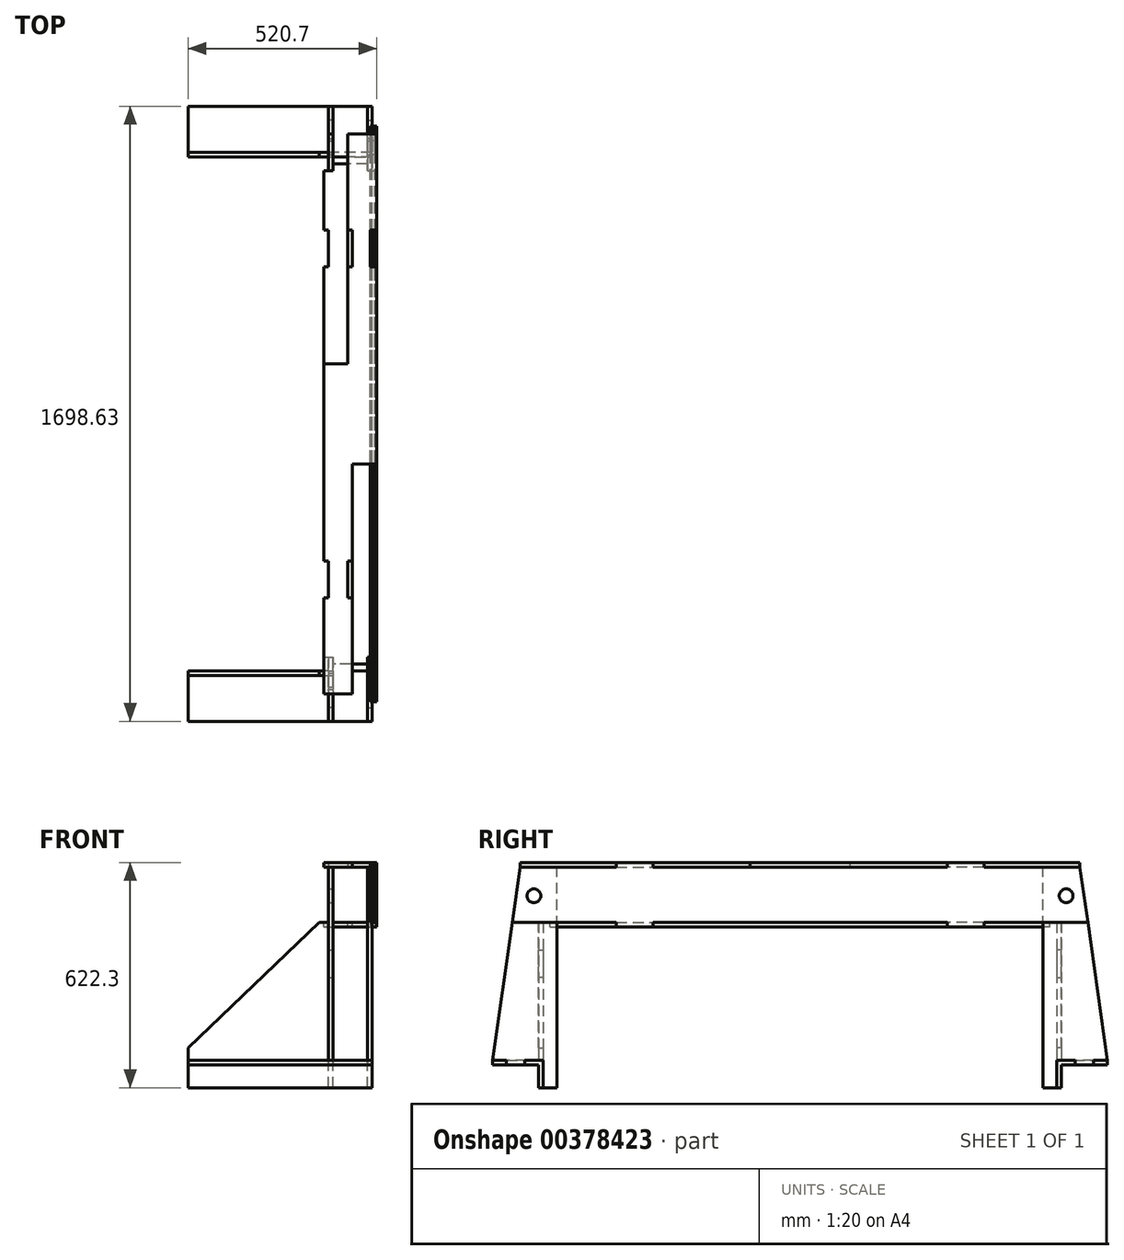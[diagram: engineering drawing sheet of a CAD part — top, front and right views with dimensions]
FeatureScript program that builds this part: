
annotation { "Feature Type Name" : "Feature", "Feature Type Description" : "" }
export const myFeature = defineFeature(function(context is Context, id is Id, definition is map)
    precondition{}
    {
        {
            var Q0;
            Q0=qCreatedBy(makeId("Top.planeOp"),FACE);
            var sketch = newSketch(context, id + "F0", { "sketchPlane" : qUnion([Q0])});
            skLineSegment(sketch, "E0", {"start": v(0, 0) * mm, "end": v(-508, 0) * mm});
            skLineSegment(sketch, "E1", {"start": v(-508, 0) * mm, "end": v(-508, 127) * mm});
            skLineSegment(sketch, "E2", {"start": v(-508, 127) * mm, "end": v(0, 127) * mm});
            skLineSegment(sketch, "E3", {"start": v(0, 127) * mm, "end": v(0, 0) * mm});
            skLineSegment(sketch, "E4.0", {"start": v(-12.7, 127) * mm, "end": v(-12.7, 0) * mm, "construction": true});
            skPoint(sketch, "E5", {"position": v(-12.7, 63.5) * mm});
            skPoint(sketch, "E6", {"position": v(-12.7, 38.1) * mm});
            skPoint(sketch, "E7", {"position": v(-12.7, 88.9) * mm});
            skLineSegment(sketch, "E8", {"start": v(-12.7, 88.9) * mm, "end": v(0, 88.9) * mm});
            skLineSegment(sketch, "E9", {"start": v(-12.7, 38.1) * mm, "end": v(0, 38.1) * mm});
            skLineSegment(sketch, "E10", {"start": v(-12.7, 88.9) * mm, "end": v(-12.7, 38.1) * mm});
            skLineSegment(sketch, "E11.0", {"start": v(-107.95, 127) * mm, "end": v(-107.95, 0) * mm, "construction": true});
            skLineSegment(sketch, "E12", {"start": v(-107.95, 88.9) * mm, "end": v(-107.95, 38.1) * mm, "construction": true});
            skLineSegment(sketch, "E13", {"start": v(-107.95, 88.9) * mm, "end": v(-120.65, 88.9) * mm});
            skLineSegment(sketch, "E14", {"start": v(-120.65, 88.9) * mm, "end": v(-120.65, 38.1) * mm});
            skLineSegment(sketch, "E15", {"start": v(-120.65, 38.1) * mm, "end": v(-107.95, 38.1) * mm});
            skLineSegment(sketch, "E16", {"start": v(-107.95, 88.9) * mm, "end": v(-107.95, 38.1) * mm});
            skSolve(sketch);
        }
        {
            var Q0;
            Q0=makeQuery(id+"F0.imprint","IMPRINT",FACE,{"disambiguationData":[TD([[makeQuery(id+"F0.imprint","IMPRINT",EDGE,{"derivedFrom":sQuery(id+"F0.wireOp",EDGE,"E0")}),-1.0]])]});
            extrude(context, id + "F1", {"entities" : qUnion([Q0]), "depth" : 12.7 * mm});
        }
        {
            var Q0;
            Q0=makeQuery(id+"F1.opExtrude","SWEPT_FACE",FACE,{"disambiguationData":[OSD([sQuery(id+"F0.wireOp",EDGE,"E0")])]});
            var sketch = newSketch(context, id + "F2", { "sketchPlane" : qUnion([Q0])});
            skLineSegment(sketch, "E17.0", {"start": v(0, 12.7) * mm, "end": v(-508, 12.7) * mm});
            skLineSegment(sketch, "E18", {"start": v(-508, 12.7) * mm, "end": v(-508, -63.5) * mm});
            skPoint(sketch, "E18.endSnap0", {"position": v(-508, 6.35) * mm});
            skLineSegment(sketch, "E19", {"start": v(-508, -63.5) * mm, "end": v(0, -63.5) * mm});
            skLineSegment(sketch, "E20", {"start": v(0, -63.5) * mm, "end": v(0, 12.7) * mm});
            skLineSegment(sketch, "E21.0", {"start": v(0, 0) * mm, "end": v(-508, 0) * mm, "construction": true});
            skPoint(sketch, "E22", {"position": v(-457.2, 0) * mm});
            skPoint(sketch, "E23", {"position": v(-381, 0) * mm});
            skPoint(sketch, "E24", {"position": v(-50.8, 0) * mm});
            skPoint(sketch, "E25", {"position": v(-127, 0) * mm});
            skLineSegment(sketch, "E26", {"start": v(-457.2, 0) * mm, "end": v(-381, 0) * mm});
            skLineSegment(sketch, "E27", {"start": v(-381, 0) * mm, "end": v(-381, 12.7) * mm});
            skLineSegment(sketch, "E28", {"start": v(-457.2, 0) * mm, "end": v(-457.2, 12.7) * mm});
            skLineSegment(sketch, "E29", {"start": v(-127, 0) * mm, "end": v(-50.8, 0) * mm});
            skLineSegment(sketch, "E30", {"start": v(-50.8, 0) * mm, "end": v(-50.8, 12.7) * mm});
            skLineSegment(sketch, "E31", {"start": v(-127, 0) * mm, "end": v(-127, 12.7) * mm});
            skSolve(sketch);
        }
        {
            var Q0;
            {var subQ3=sQuery(id+"F2.wireOp",EDGE,"E19");Q0=makeQuery(id+"F2.imprint","IMPRINT",FACE,{"disambiguationData":[TD([[makeQuery(id+"F2.imprint","IMPRINT",EDGE,{"derivedFrom":subQ3}),1.0]])]});}
            var Q1;
            {var subQ3=sQuery(id+"F2.wireOp",EDGE,"E28");Q1=makeQuery(id+"F2.imprint","IMPRINT",FACE,{"disambiguationData":[TD([[makeQuery(id+"F2.imprint","IMPRINT",EDGE,{"derivedFrom":subQ3}),1.0]])]});}
            var Q2;
            {var subQ3=sQuery(id+"F2.wireOp",EDGE,"E27");Q2=makeQuery(id+"F2.imprint","IMPRINT",FACE,{"disambiguationData":[TD([[makeQuery(id+"F2.imprint","IMPRINT",EDGE,{"derivedFrom":subQ3}),-1.0]])]});}
            var Q3;
            {var subQ3=sQuery(id+"F2.wireOp",EDGE,"E30");Q3=makeQuery(id+"F2.imprint","IMPRINT",FACE,{"disambiguationData":[TD([[makeQuery(id+"F2.imprint","IMPRINT",EDGE,{"derivedFrom":subQ3}),-1.0]])]});}
            extrude(context, id + "F3", {"entities" : qUnion([Q0, Q1, Q2, Q3]), "depth" : 12.7 * mm});
        }
        {
            var Q0;
            Q0=makeQuery(id+"F2.imprint","IMPRINT",FACE,{"disambiguationData":[TD([[makeQuery(id+"F2.imprint","IMPRINT",EDGE,{"derivedFrom":sQuery(id+"F2.wireOp",EDGE,"E26")}),-1.0]])]});
            var Q1;
            Q1=makeQuery(id+"F2.imprint","IMPRINT",FACE,{"disambiguationData":[TD([[makeQuery(id+"F2.imprint","IMPRINT",EDGE,{"derivedFrom":sQuery(id+"F2.wireOp",EDGE,"E29")}),-1.0]])]});
            var Q2;
            Q2=makeQuery(id+"F3.opExtrude","CAP_FACE",FACE,{"disambiguationData":[OSD([sQuery(id+"F2.wireOp",EDGE,"E17.0"),sQuery(id+"F2.wireOp",EDGE,"E18"),sQuery(id+"F2.wireOp",EDGE,"E19"),sQuery(id+"F2.wireOp",EDGE,"E20"),sQuery(id+"F2.wireOp",EDGE,"E26"),sQuery(id+"F2.wireOp",EDGE,"E27"),sQuery(id+"F2.wireOp",EDGE,"E28"),sQuery(id+"F2.wireOp",EDGE,"E29"),sQuery(id+"F2.wireOp",EDGE,"E30"),sQuery(id+"F2.wireOp",EDGE,"E31")])],"isStart":false});
            extrude(context, id + "F4", {"entities" : qUnion([Q0, Q1]), "operationType" : NewBodyOperationType.ADD, "endBound" : BoundingType.UP_TO_SURFACE, "endBoundEntityFace" : qUnion([Q2]), "depth" : 25.4 * mm});
        }
        {
            var Q0;
            Q0=makeQuery(id+"F1.opExtrude","SWEPT_FACE",FACE,{"disambiguationData":[OSD([sQuery(id+"F0.wireOp",EDGE,"E3")])]});
            var sketch = newSketch(context, id + "F5", { "sketchPlane" : qUnion([Q0])});
            skLineSegment(sketch, "E32.0", {"start": v(-12.7, -63.5) * mm, "end": v(-12.7, 12.7) * mm});
            skLineSegment(sketch, "E33.0", {"start": v(127, 12.7) * mm, "end": v(88.9, 12.7) * mm});
            skLineSegment(sketch, "E34", {"start": v(-12.7, 12.7) * mm, "end": v(38.1, 12.7) * mm});
            skLineSegment(sketch, "E35", {"start": v(-12.7, -63.5) * mm, "end": v(-50.8, -63.5) * mm});
            skLineSegment(sketch, "E36", {"start": v(-50.8, -63.5) * mm, "end": v(-50.8, 546.1) * mm});
            skLineSegment(sketch, "E37", {"start": v(-50.8, 546.1) * mm, "end": v(50.8, 546.1) * mm});
            skLineSegment(sketch, "E38", {"start": v(50.8, 546.1) * mm, "end": v(127, 12.7) * mm});
            skCircle(sketch, "E39", {"center": v(12.7, 466.73) * mm, "radius": 19.05 * mm});
            skLineSegment(sketch, "E40", {"start": v(12.7, 466.73) * mm, "end": v(-50.8, 466.73) * mm});
            skLineSegment(sketch, "E41", {"start": v(12.7, 466.73) * mm, "end": v(12.7, 546.1) * mm});
            skLineSegment(sketch, "E42.0", {"start": v(88.9, 0) * mm, "end": v(38.1, 0) * mm});
            skLineSegment(sketch, "E43", {"start": v(88.9, 0) * mm, "end": v(88.9, 12.7) * mm});
            skLineSegment(sketch, "E44", {"start": v(38.1, 0) * mm, "end": v(38.1, 12.7) * mm});
            skSolve(sketch);
        }
        {
            var Q0;
            Q0=makeQuery(id+"F5.imprint","IMPRINT",FACE,{"disambiguationData":[TD([[makeQuery(id+"F5.imprint","IMPRINT",EDGE,{"derivedFrom":sQuery(id+"F5.wireOp",EDGE,"E32.0")}),1.0]])]});
            var Q1;
            {var subQ1=sQuery(id+"F5.wireOp",EDGE,"E36");var subQ7=sQuery(id+"F5.wireOp",EDGE,"E37");var subQ8=makeQuery(id+"F5.imprint","INTERSECT",VERTEX,{"derivedFrom":[subQ1,subQ7]});Q1=makeQuery(id+"F5.imprint","IMPRINT",FACE,{"disambiguationData":[TD([[makeQuery(id+"F5.imprint","IMPRINT",EDGE,{"disambiguationData":[TD([[subQ8,1.0]])],"derivedFrom":subQ1}),-1.0]])]});}
            extrude(context, id + "F6", {"entities" : qUnion([Q0, Q1]), "oppositeDirection" : true, "depth" : 12.7 * mm});
        }
        {
            assignVariable(context, id + "F7", {"name" : "BW", "anyValue" : 4.25});
        }
        {
            var Q0;
            Q0=makeQuery(id+"F1.opExtrude","SWEPT_FACE",FACE,{"disambiguationData":[OSD([sQuery(id+"F0.wireOp",EDGE,"E16")])]});
            cPlane(context, id + "F8", {"entities" : qUnion([Q0]), "cplaneType" : CPlaneType.OFFSET, "offset" : 0 * mm, "oppositeDirection" : true, "width" : 152.4 * mm, "height" : 152.4 * mm});
        }
        {
            var Q0;
            Q0=qCreatedBy(id+"F8.planeOp",FACE);
            var sketch = newSketch(context, id + "F9", { "sketchPlane" : qUnion([Q0])});
            skLineSegment(sketch, "E45.0", {"start": v(50.8, 546.1) * mm, "end": v(-50.8, 546.1) * mm});
            skLineSegment(sketch, "E46.0", {"start": v(-50.8, 546.1) * mm, "end": v(-127, 12.7) * mm});
            skLineSegment(sketch, "E47.0", {"start": v(50.8, -63.5) * mm, "end": v(50.8, 546.1) * mm});
            skLineSegment(sketch, "E48.0", {"start": v(12.7, -63.5) * mm, "end": v(50.8, -63.5) * mm});
            skLineSegment(sketch, "E49.0", {"start": v(12.7, -63.5) * mm, "end": v(12.7, 12.7) * mm});
            skLineSegment(sketch, "E50.0", {"start": v(12.7, 12.7) * mm, "end": v(-38.1, 12.7) * mm});
            skPoint(sketch, "E51.0", {"position": v(-38.1, 6.35) * mm});
            skLineSegment(sketch, "E52.0", {"start": v(-88.9, 0) * mm, "end": v(-38.1, 0) * mm});
            skPoint(sketch, "E53.0", {"position": v(-88.9, 6.35) * mm});
            skLineSegment(sketch, "E54.0", {"start": v(-127, 12.7) * mm, "end": v(-88.9, 12.7) * mm});
            skLineSegment(sketch, "E55.0", {"start": v(-88.9, 0) * mm, "end": v(-88.9, 12.7) * mm});
            skLineSegment(sketch, "E56.0", {"start": v(-38.1, 0) * mm, "end": v(-38.1, 12.7) * mm});
            skLineSegment(sketch, "E57", {"start": v(12.7, 12.7) * mm, "end": v(12.7, 546.1) * mm, "construction": true});
            skLineSegment(sketch, "E58.0", {"start": v(0, 12.7) * mm, "end": v(0, 546.1) * mm, "construction": true});
            skPoint(sketch, "E59", {"position": v(12.7, 241.3) * mm});
            skLineSegment(sketch, "E60", {"start": v(12.7, 241.3) * mm, "end": v(0, 241.3) * mm});
            skPoint(sketch, "E60.endSnap0", {"position": v(0, 279.4) * mm});
            skLineSegment(sketch, "E61", {"start": v(0, 241.3) * mm, "end": v(0, 317.5) * mm});
            skLineSegment(sketch, "E62", {"start": v(0, 317.5) * mm, "end": v(12.7, 317.5) * mm});
            skLineSegment(sketch, "E63", {"start": v(12.7, 317.5) * mm, "end": v(12.7, 241.3) * mm});
            skCircle(sketch, "E64.0", {"center": v(-12.7, 466.73) * mm, "radius": 19.05 * mm});
            skSolve(sketch);
        }
        {
            var Q0;
            Q0=makeQuery(id+"F9.imprint","IMPRINT",FACE,{"disambiguationData":[TD([[makeQuery(id+"F9.imprint","IMPRINT",EDGE,{"derivedFrom":sQuery(id+"F9.wireOp",EDGE,"E45.0")}),1.0]])]});
            extrude(context, id + "F10", {"entities" : qUnion([Q0]), "depth" : 12.7 * mm});
        }
        {
            var Q0;
            {var subQ0=sQuery(id+"F2.wireOp",EDGE,"E17.0");Q0=makeQuery(id+"F3.opExtrude","SWEPT_FACE",FACE,{"disambiguationData":[OSD([subQ0]),TDD([makeQuery(id+"F2.imprint","IMPRINT",EDGE,{"disambiguationData":[TD([[makeQuery(id+"F2.imprint","INTERSECT",VERTEX,{"derivedFrom":[subQ0,sQuery(id+"F2.wireOp",EDGE,"E27")]}),1.0]])],"derivedFrom":subQ0})])]});}
            var sketch = newSketch(context, id + "F11", { "sketchPlane" : qUnion([Q0])});
            skLineSegment(sketch, "E65.0", {"start": v(-120.65, -12.7) * mm, "end": v(-120.65, 38.1) * mm});
            skLineSegment(sketch, "E66.0", {"start": v(-508, -12.7) * mm, "end": v(-508, 0) * mm});
            skLineSegment(sketch, "E67", {"start": v(-508, -12.7) * mm, "end": v(-120.65, -12.7) * mm});
            skLineSegment(sketch, "E68", {"start": v(-508, 0) * mm, "end": v(-120.65, 0) * mm});
            skSolve(sketch);
        }
        {
            var Q0;
            Q0=makeQuery(id+"F11.imprint","IMPRINT",FACE,{"disambiguationData":[TD([[makeQuery(id+"F11.imprint","IMPRINT",EDGE,{"derivedFrom":sQuery(id+"F11.wireOp",EDGE,"c8208c28-5663-4249-825d-4aff4fe314d8.0")}),1.0]])]});
            var Q1;
            {var subQ1=sQuery(id+"F2.wireOp",EDGE,"E17.0");var subQ2=makeQuery(id+"F3.opExtrude","SWEPT_EDGE",EDGE,{"disambiguationData":[OSD([subQ1,sQuery(id+"F2.wireOp",EDGE,"E27")])]});Q1=makeQuery(id+"F11.imprint","IMPRINT",FACE,{"disambiguationData":[TD([[makeQuery(id+"F11.imprint","IMPRINT",EDGE,{"derivedFrom":subQ2}),-1.0]])]});}
            var Q2;
            {var subQ0=sQuery(id+"F11.wireOp",EDGE,"E66.0");Q2=makeQuery(id+"F11.imprint","IMPRINT",FACE,{"disambiguationData":[TD([[makeQuery(id+"F11.imprint","IMPRINT",EDGE,{"derivedFrom":subQ0}),-1.0]])]});}
            var Q3;
            {var subQ5=makeQuery(id+"F3.opExtrude","SWEPT_EDGE",EDGE,{"disambiguationData":[OSD([sQuery(id+"F2.wireOp",EDGE,"E17.0"),sQuery(id+"F2.wireOp",EDGE,"E31")])]});Q3=makeQuery(id+"F11.imprint","IMPRINT",FACE,{"disambiguationData":[TD([[makeQuery(id+"F11.imprint","IMPRINT",EDGE,{"derivedFrom":subQ5}),-1.0]])]});}
            extrude(context, id + "F12", {"entities" : qUnion([Q0, Q1, Q2, Q3]), "depth" : 381 * mm});
        }
        {
            var Q0;
            Q0=makeQuery(id+"F12.opExtrude","SWEPT_FACE",FACE,{"disambiguationData":[OSD([sQuery(id+"F11.wireOp",EDGE,"E67")])]});
            var sketch = newSketch(context, id + "F13", { "sketchPlane" : qUnion([Q0])});
            skLineSegment(sketch, "E69.0", {"start": v(-508, 12.7) * mm, "end": v(-120.65, 12.7) * mm});
            skLineSegment(sketch, "E70", {"start": v(-508, 12.7) * mm, "end": v(-508, 46.36) * mm});
            skLineSegment(sketch, "E71", {"start": v(-120.65, 393.7) * mm, "end": v(-146.05, 393.7) * mm});
            skLineSegment(sketch, "E72", {"start": v(-146.05, 393.7) * mm, "end": v(-508, 46.36) * mm});
            skSolve(sketch);
        }
        {
            var Q0;
            Q0=makeQuery(id+"F9.imprint","IMPRINT",FACE,{"disambiguationData":[TD([[makeQuery(id+"F9.imprint","IMPRINT",EDGE,{"derivedFrom":sQuery(id+"F9.wireOp",EDGE,"E60")}),-1.0]])]});
            extrude(context, id + "F14", {"entities" : qUnion([Q0]), "endBound" : BoundingType.UP_TO_NEXT, "depth" : 25.4 * mm});
        }
        {
            var Q0;
            {var subQ0=sQuery(id+"F13.wireOp",EDGE,"E72");Q0=makeQuery(id+"F13.imprint","IMPRINT",FACE,{"disambiguationData":[TD([[makeQuery(id+"F13.imprint","IMPRINT",EDGE,{"derivedFrom":subQ0}),-1.0]])]});}
            extrude(context, id + "F15", {"entities" : qUnion([Q0]), "operationType" : NewBodyOperationType.REMOVE, "oppositeDirection" : true, "depth" : 25.4 * mm});
        }
        {
            var Q0;
            Q0=makeQuery(id+"F5.imprint","IMPRINT",FACE,{"disambiguationData":[TD([[makeQuery(id+"F5.imprint","IMPRINT",EDGE,{"derivedFrom":sQuery(id+"F5.wireOp",EDGE,"E39")}),1.0]])]});
            extrude(context, id + "F16", {"entities" : qUnion([Q0]), "oppositeDirection" : true, "depth" : (getVariable(context, 'BW') + 1) * mm});
        }
        {
            var Q0;
            Q0=qCreatedBy(makeId("Front.planeOp"),FACE);
            cPlane(context, id + "F17", {"entities" : qUnion([Q0]), "cplaneType" : CPlaneType.OFFSET, "offset" : 722.3 * mm, "width" : 152.4 * mm, "height" : 152.4 * mm});
        }
        {
            var Q0;
            Q0=makeQuery(id+"F1.opExtrude","SWEPT_BODY",BODY,{"disambiguationData":[OSD([sQuery(id+"F0.wireOp",EDGE,"E0"),sQuery(id+"F0.wireOp",EDGE,"E1"),sQuery(id+"F0.wireOp",EDGE,"E2"),sQuery(id+"F0.wireOp",EDGE,"E3"),sQuery(id+"F0.wireOp",EDGE,"E8"),sQuery(id+"F0.wireOp",EDGE,"E9"),sQuery(id+"F0.wireOp",EDGE,"E10"),sQuery(id+"F0.wireOp",EDGE,"E13"),sQuery(id+"F0.wireOp",EDGE,"E14"),sQuery(id+"F0.wireOp",EDGE,"E15"),sQuery(id+"F0.wireOp",EDGE,"E16")])]});
            var Q1;
            Q1=makeQuery(id+"F16.opExtrude","SWEPT_BODY",BODY,{"disambiguationData":[OSD([sQuery(id+"F5.wireOp",EDGE,"E39")])]});
            var Q2;
            Q2=makeQuery(id+"F10.opExtrude","SWEPT_BODY",BODY,{"disambiguationData":[OSD([sQuery(id+"F9.wireOp",EDGE,"E45.0"),sQuery(id+"F9.wireOp",EDGE,"E46.0"),sQuery(id+"F9.wireOp",EDGE,"E47.0"),sQuery(id+"F9.wireOp",EDGE,"E48.0"),sQuery(id+"F9.wireOp",EDGE,"E49.0"),sQuery(id+"F9.wireOp",EDGE,"E50.0"),sQuery(id+"F9.wireOp",EDGE,"E52.0"),sQuery(id+"F9.wireOp",EDGE,"E54.0"),sQuery(id+"F9.wireOp",EDGE,"E55.0"),sQuery(id+"F9.wireOp",EDGE,"E56.0")])]});
            var Q3;
            Q3=makeQuery(id+"F12.opExtrude","SWEPT_BODY",BODY,{"disambiguationData":[OSD([sQuery(id+"F11.wireOp",EDGE,"E65.0"),sQuery(id+"F11.wireOp",EDGE,"E66.0"),sQuery(id+"F11.wireOp",EDGE,"E67"),sQuery(id+"F11.wireOp",EDGE,"E68")])]});
            var Q4;
            Q4=makeQuery(id+"F6.opExtrude","SWEPT_BODY",BODY,{"disambiguationData":[OSD([sQuery(id+"F5.wireOp",EDGE,"E32.0"),sQuery(id+"F5.wireOp",EDGE,"E33.0"),sQuery(id+"F5.wireOp",EDGE,"E34"),sQuery(id+"F5.wireOp",EDGE,"E35"),sQuery(id+"F5.wireOp",EDGE,"E36"),sQuery(id+"F5.wireOp",EDGE,"E37"),sQuery(id+"F5.wireOp",EDGE,"E38"),sQuery(id+"F5.wireOp",EDGE,"E39"),sQuery(id+"F5.wireOp",EDGE,"E42.0"),sQuery(id+"F5.wireOp",EDGE,"E43"),sQuery(id+"F5.wireOp",EDGE,"E44")])]});
            var Q5;
            Q5=makeQuery(id+"F3.opExtrude","SWEPT_BODY",BODY,{"disambiguationData":[OSD([sQuery(id+"F2.wireOp",EDGE,"E17.0"),sQuery(id+"F2.wireOp",EDGE,"E18"),sQuery(id+"F2.wireOp",EDGE,"E19"),sQuery(id+"F2.wireOp",EDGE,"E20"),sQuery(id+"F2.wireOp",EDGE,"E26"),sQuery(id+"F2.wireOp",EDGE,"E27"),sQuery(id+"F2.wireOp",EDGE,"E28"),sQuery(id+"F2.wireOp",EDGE,"E29"),sQuery(id+"F2.wireOp",EDGE,"E30"),sQuery(id+"F2.wireOp",EDGE,"E31")])]});
            var Q6;
            Q6=qCreatedBy(id+"F17.planeOp",FACE);
            mirror(context, id + "F18", {"entities" : qUnion([Q0, Q1, Q2, Q3, Q4, Q5]), "mirrorPlane" : qUnion([Q6])});
        }
        {
            var Q0;
            Q0=makeQuery(id+"F18.opPattern","COPY",FACE,{"derivedFrom":makeQuery(id+"F6.opExtrude","CAP_FACE",FACE,{"disambiguationData":[OSD([sQuery(id+"F5.wireOp",EDGE,"E32.0"),sQuery(id+"F5.wireOp",EDGE,"E33.0"),sQuery(id+"F5.wireOp",EDGE,"E34"),sQuery(id+"F5.wireOp",EDGE,"E35"),sQuery(id+"F5.wireOp",EDGE,"E36"),sQuery(id+"F5.wireOp",EDGE,"E37"),sQuery(id+"F5.wireOp",EDGE,"E38"),sQuery(id+"F5.wireOp",EDGE,"E39")])],"isStart":true}),"instanceName":"1"});
            var sketch = newSketch(context, id + "F19", { "sketchPlane" : qUnion([Q0])});
            skLineSegment(sketch, "E73.0", {"start": v(-1495.42, 546.1) * mm, "end": v(-1517.2, 393.7) * mm});
            skLineSegment(sketch, "E74.0", {"start": v(50.8, 546.1) * mm, "end": v(72.57, 393.7) * mm});
            skCircle(sketch, "E75.0", {"center": v(12.7, 466.73) * mm, "radius": 19.05 * mm});
            skCircle(sketch, "E76.0", {"center": v(-1457.33, 466.73) * mm, "radius": 19.05 * mm});
            skLineSegment(sketch, "E77", {"start": v(-1495.42, 546.1) * mm, "end": v(50.8, 546.1) * mm});
            skLineSegment(sketch, "E78.0", {"start": v(-1517.2, 393.7) * mm, "end": v(72.57, 393.7) * mm});
            skPoint(sketch, "E79.orphan", {"position": v(-1571.62, 12.7) * mm});
            skPoint(sketch, "E80.orphan", {"position": v(127, 12.7) * mm});
            skLineSegment(sketch, "E81.0", {"start": v(-1230.31, 558.8) * mm, "end": v(-1128.71, 558.8) * mm});
            skLineSegment(sketch, "E82.0", {"start": v(-1230.31, 381) * mm, "end": v(-1128.71, 381) * mm});
            skLineSegment(sketch, "E83", {"start": v(-722.31, 546.1) * mm, "end": v(-722.31, 393.7) * mm, "construction": true});
            skLineSegment(sketch, "E84", {"start": v(-722.31, 469.9) * mm, "end": v(-315.91, 469.9) * mm, "construction": true});
            skLineSegment(sketch, "E85", {"start": v(-315.91, 469.9) * mm, "end": v(-722.31, 469.9) * mm, "construction": true});
            skLineSegment(sketch, "E86", {"start": v(-722.31, 469.9) * mm, "end": v(-1128.71, 469.9) * mm, "construction": true});
            skLineSegment(sketch, "E87", {"start": v(-315.91, 469.9) * mm, "end": v(-265.11, 469.9) * mm, "construction": true});
            skLineSegment(sketch, "E88", {"start": v(-265.11, 469.9) * mm, "end": v(-214.31, 469.9) * mm, "construction": true});
            skLineSegment(sketch, "E89", {"start": v(-1128.71, 469.9) * mm, "end": v(-1179.51, 469.9) * mm, "construction": true});
            skLineSegment(sketch, "E90", {"start": v(-1179.51, 469.9) * mm, "end": v(-1230.31, 469.9) * mm, "construction": true});
            skLineSegment(sketch, "E91", {"start": v(-214.31, 469.9) * mm, "end": v(-214.31, 558.8) * mm});
            skLineSegment(sketch, "E92", {"start": v(-315.91, 469.9) * mm, "end": v(-315.91, 558.8) * mm});
            skLineSegment(sketch, "E93", {"start": v(-315.91, 469.9) * mm, "end": v(-315.91, 381) * mm});
            skLineSegment(sketch, "E94", {"start": v(-214.31, 469.9) * mm, "end": v(-214.31, 381) * mm});
            skLineSegment(sketch, "E95", {"start": v(-1230.31, 469.9) * mm, "end": v(-1230.31, 558.8) * mm});
            skLineSegment(sketch, "E96", {"start": v(-1128.71, 469.9) * mm, "end": v(-1128.71, 558.8) * mm});
            skLineSegment(sketch, "E97", {"start": v(-1128.71, 469.9) * mm, "end": v(-1128.71, 381) * mm});
            skLineSegment(sketch, "E98", {"start": v(-1230.31, 469.9) * mm, "end": v(-1230.31, 381) * mm});
            skLineSegment(sketch, "E99.trimOffspring", {"start": v(-315.91, 558.8) * mm, "end": v(-214.31, 558.8) * mm});
            skLineSegment(sketch, "E100.trimOffspring", {"start": v(-315.91, 381) * mm, "end": v(-214.31, 381) * mm});
            skSolve(sketch);
        }
        {
            var Q0;
            {var subQ1=sQuery(id+"F19.wireOp",EDGE,"E74.0");Q0=makeQuery(id+"F19.imprint","IMPRINT",FACE,{"disambiguationData":[TD([[makeQuery(id+"F19.imprint","IMPRINT",EDGE,{"derivedFrom":subQ1}),-1.0]])]});}
            var Q1;
            {var subQ1=sQuery(id+"F19.wireOp",EDGE,"E73.0");Q1=makeQuery(id+"F19.imprint","IMPRINT",FACE,{"disambiguationData":[TD([[makeQuery(id+"F19.imprint","IMPRINT",EDGE,{"derivedFrom":subQ1}),1.0]])]});}
            var Q2;
            {var subQ1=sQuery(id+"F19.wireOp",EDGE,"E92");var subQ3=sQuery(id+"F19.wireOp",EDGE,"E77");var subQ4=makeQuery(id+"F19.imprint","INTERSECT",VERTEX,{"derivedFrom":[subQ3,subQ1]});Q2=makeQuery(id+"F19.imprint","IMPRINT",FACE,{"disambiguationData":[TD([[makeQuery(id+"F19.imprint","IMPRINT",EDGE,{"disambiguationData":[TD([[subQ4,-1.0]])],"derivedFrom":subQ3}),-1.0]])]});}
            var Q3;
            {var subQ5=sQuery(id+"F19.wireOp",EDGE,"E99.trimOffspring");Q3=makeQuery(id+"F19.imprint","IMPRINT",FACE,{"disambiguationData":[TD([[makeQuery(id+"F19.imprint","IMPRINT",EDGE,{"derivedFrom":subQ5}),-1.0]])]});}
            var Q4;
            {var subQ5=sQuery(id+"F19.wireOp",EDGE,"E100.trimOffspring");Q4=makeQuery(id+"F19.imprint","IMPRINT",FACE,{"disambiguationData":[TD([[makeQuery(id+"F19.imprint","IMPRINT",EDGE,{"derivedFrom":subQ5}),1.0]])]});}
            var Q5;
            {var subQ7=sQuery(id+"F19.wireOp",EDGE,"E77");var subQ9=sQuery(id+"F19.wireOp",EDGE,"E96");var subQ10=makeQuery(id+"F19.imprint","INTERSECT",VERTEX,{"derivedFrom":[subQ7,subQ9]});Q5=makeQuery(id+"F19.imprint","IMPRINT",FACE,{"disambiguationData":[TD([[makeQuery(id+"F19.imprint","IMPRINT",EDGE,{"disambiguationData":[TD([[subQ10,-1.0]])],"derivedFrom":subQ7}),-1.0]])]});}
            var Q6;
            {var subQ1=sQuery(id+"F19.wireOp",EDGE,"E95");var subQ3=sQuery(id+"F19.wireOp",EDGE,"E77");var subQ4=makeQuery(id+"F19.imprint","INTERSECT",VERTEX,{"derivedFrom":[subQ3,subQ1]});Q6=makeQuery(id+"F19.imprint","IMPRINT",FACE,{"disambiguationData":[TD([[makeQuery(id+"F19.imprint","IMPRINT",EDGE,{"disambiguationData":[TD([[subQ4,-1.0]])],"derivedFrom":subQ3}),-1.0]])]});}
            var Q7;
            {var subQ5=sQuery(id+"F19.wireOp",EDGE,"E81.0");Q7=makeQuery(id+"F19.imprint","IMPRINT",FACE,{"disambiguationData":[TD([[makeQuery(id+"F19.imprint","IMPRINT",EDGE,{"derivedFrom":subQ5}),-1.0]])]});}
            var Q8;
            {var subQ5=sQuery(id+"F19.wireOp",EDGE,"E82.0");Q8=makeQuery(id+"F19.imprint","IMPRINT",FACE,{"disambiguationData":[TD([[makeQuery(id+"F19.imprint","IMPRINT",EDGE,{"derivedFrom":subQ5}),1.0]])]});}
            var Q9;
            {var subQ1=sQuery(id+"F19.wireOp",EDGE,"E95");var subQ5=sQuery(id+"F19.wireOp",EDGE,"E77");var subQ9=makeQuery(id+"F19.imprint","INTERSECT",VERTEX,{"derivedFrom":[subQ5,subQ1]});Q9=makeQuery(id+"F19.imprint","IMPRINT",FACE,{"disambiguationData":[TD([[makeQuery(id+"F19.imprint","IMPRINT",EDGE,{"disambiguationData":[TD([[subQ9,1.0]])],"derivedFrom":subQ5}),-1.0]])]});}
            extrude(context, id + "F20", {"entities" : qUnion([Q0, Q1, Q2, Q3, Q4, Q5, Q6, Q7, Q8, Q9]), "depth" : 12.7 * mm});
        }
        {
            var Q0;
            Q0=makeQuery(id+"F20.opExtrude","SWEPT_BODY",BODY,{"disambiguationData":[OSD([sQuery(id+"F19.wireOp",EDGE,"E73.0"),sQuery(id+"F19.wireOp",EDGE,"E74.0"),sQuery(id+"F19.wireOp",EDGE,"E75.0"),sQuery(id+"F19.wireOp",EDGE,"E76.0"),sQuery(id+"F19.wireOp",EDGE,"E77"),sQuery(id+"F19.wireOp",EDGE,"E78.0")])]});
            transform(context, id + "F21", {"entities" : qUnion([Q0]), "transformType" : TransformType.TRANSLATION_3D, "dx" : (-getVariable(context, 'BW') - 1) * mm, "dy" : 0 * mm, "dz" : 0 * mm, "makeCopy" : true});
        }
        {
            var Q0;
            Q0=makeQuery(id+"F20.opExtrude","SWEPT_FACE",FACE,{"disambiguationData":[OSD([sQuery(id+"F19.wireOp",EDGE,"E77")])]});
            var sketch = newSketch(context, id + "F22", { "sketchPlane" : qUnion([Q0])});
            skLineSegment(sketch, "E101.0", {"start": v(-133.35, -1230.31) * mm, "end": v(-133.35, -1495.42) * mm});
            skLineSegment(sketch, "E102.0", {"start": v(12.7, -214.31) * mm, "end": v(12.7, 50.8) * mm});
            skLineSegment(sketch, "E103", {"start": v(-133.35, -1495.42) * mm, "end": v(-53.97, -1495.42) * mm});
            skLineSegment(sketch, "E104", {"start": v(12.7, 50.8) * mm, "end": v(-66.68, 50.8) * mm});
            skLineSegment(sketch, "E105", {"start": v(-53.97, -1495.42) * mm, "end": v(-53.98, -860.42) * mm});
            skLineSegment(sketch, "E106", {"start": v(-66.68, 50.8) * mm, "end": v(-66.67, -584.2) * mm});
            skLineSegment(sketch, "E107", {"start": v(-66.67, -584.2) * mm, "end": v(-133.35, -584.2) * mm});
            skLineSegment(sketch, "E108", {"start": v(-53.98, -860.42) * mm, "end": v(12.7, -860.42) * mm});
            skLineSegment(sketch, "E109", {"start": v(12.7, -860.42) * mm, "end": v(12.7, -315.91) * mm});
            skLineSegment(sketch, "E110", {"start": v(-133.35, -1128.71) * mm, "end": v(-133.35, -584.2) * mm});
            skLineSegment(sketch, "E111.0.1", {"start": v(-133.35, -1230.31) * mm, "end": v(-120.65, -1230.31) * mm});
            skLineSegment(sketch, "E111.0.2", {"start": v(-120.65, -1230.31) * mm, "end": v(-120.65, -1128.71) * mm});
            skLineSegment(sketch, "E111.0.3", {"start": v(-120.65, -1128.71) * mm, "end": v(-133.35, -1128.71) * mm});
            skLineSegment(sketch, "E112.0.0", {"start": v(0, -214.31) * mm, "end": v(0, -315.91) * mm});
            skLineSegment(sketch, "E112.0.1", {"start": v(0, -315.91) * mm, "end": v(12.7, -315.91) * mm});
            skLineSegment(sketch, "E112.0.3", {"start": v(12.7, -214.31) * mm, "end": v(0, -214.31) * mm});
            skLineSegment(sketch, "E113.0", {"start": v(-66.68, -1230.31) * mm, "end": v(-66.68, -1128.71) * mm});
            skLineSegment(sketch, "E114.0", {"start": v(-53.97, -214.31) * mm, "end": v(-53.97, -315.91) * mm});
            skLineSegment(sketch, "E115", {"start": v(-66.68, -1128.71) * mm, "end": v(-53.98, -1128.71) * mm});
            skLineSegment(sketch, "E116", {"start": v(-66.68, -1230.31) * mm, "end": v(-53.98, -1230.31) * mm});
            skLineSegment(sketch, "E117", {"start": v(-53.97, -315.91) * mm, "end": v(-66.67, -315.91) * mm});
            skLineSegment(sketch, "E118", {"start": v(-66.67, -315.91) * mm, "end": v(-64.72, -320.22) * mm});
            skLineSegment(sketch, "E119", {"start": v(-53.97, -214.31) * mm, "end": v(-66.67, -214.31) * mm});
            skLineSegment(sketch, "E120", {"start": v(-66.67, -214.31) * mm, "end": v(-62.67, -216.1) * mm});
            skSolve(sketch);
        }
        {
            var Q0;
            Q0=makeQuery(id+"F22.imprint","IMPRINT",FACE,{"disambiguationData":[TD([[makeQuery(id+"F22.imprint","IMPRINT",EDGE,{"derivedFrom":sQuery(id+"F22.wireOp",EDGE,"E101.0")}),1.0]])]});
            var Q1;
            {var subQ0=sQuery(id+"F22.wireOp",EDGE,"E109");Q1=makeQuery(id+"F22.imprint","IMPRINT",FACE,{"disambiguationData":[TD([[makeQuery(id+"F22.imprint","IMPRINT",EDGE,{"derivedFrom":subQ0}),1.0]])]});}
            var Q2;
            {var subQ0=sQuery(id+"F22.wireOp",EDGE,"E102.0");Q2=makeQuery(id+"F22.imprint","IMPRINT",FACE,{"disambiguationData":[TD([[makeQuery(id+"F22.imprint","IMPRINT",EDGE,{"derivedFrom":subQ0}),1.0]])]});}
            extrude(context, id + "F23", {"entities" : qUnion([Q0, Q1, Q2]), "depth" : 12.7 * mm});
        }
        {
            var Q0;
            Q0=makeQuery(id+"F20.opExtrude","SWEPT_FACE",FACE,{"disambiguationData":[OSD([sQuery(id+"F19.wireOp",EDGE,"E78.0")])]});
            var sketch = newSketch(context, id + "F24", { "sketchPlane" : qUnion([Q0])});
            skLineSegment(sketch, "E121.0", {"start": v(-120.65, 1393.83) * mm, "end": v(-107.95, 1393.83) * mm});
            skLineSegment(sketch, "E122.0", {"start": v(-12.7, 1393.83) * mm, "end": v(0, 1393.83) * mm});
            skLineSegment(sketch, "E123.0", {"start": v(-12.7, 50.8) * mm, "end": v(0, 50.8) * mm});
            skLineSegment(sketch, "E124.0", {"start": v(-120.65, 50.8) * mm, "end": v(-107.95, 50.8) * mm});
            skLineSegment(sketch, "E125", {"start": v(-120.65, 50.8) * mm, "end": v(-133.35, 50.8) * mm});
            skLineSegment(sketch, "E126", {"start": v(0, 50.8) * mm, "end": v(12.7, 50.8) * mm});
            skLineSegment(sketch, "E127", {"start": v(-120.65, 1393.83) * mm, "end": v(-133.35, 1393.83) * mm});
            skLineSegment(sketch, "E128", {"start": v(0, 1393.83) * mm, "end": v(12.7, 1393.83) * mm});
            skPoint(sketch, "E129.orphan", {"position": v(-508, 12.7) * mm});
            skLineSegment(sketch, "E130.0.1", {"start": v(-133.35, 1128.71) * mm, "end": v(-120.65, 1128.71) * mm});
            skLineSegment(sketch, "E130.0.2", {"start": v(-120.65, 1128.71) * mm, "end": v(-120.65, 1230.31) * mm});
            skLineSegment(sketch, "E130.0.3", {"start": v(-120.65, 1230.31) * mm, "end": v(-133.35, 1230.31) * mm});
            skLineSegment(sketch, "E131.0.0", {"start": v(0, 1230.31) * mm, "end": v(0, 1128.71) * mm});
            skLineSegment(sketch, "E131.0.1", {"start": v(0, 1128.71) * mm, "end": v(12.7, 1128.71) * mm});
            skLineSegment(sketch, "E131.0.3", {"start": v(12.7, 1230.31) * mm, "end": v(0, 1230.31) * mm});
            skLineSegment(sketch, "E132.0.0", {"start": v(0, 315.91) * mm, "end": v(0, 214.31) * mm});
            skLineSegment(sketch, "E132.0.1", {"start": v(0, 214.31) * mm, "end": v(12.7, 214.31) * mm});
            skLineSegment(sketch, "E132.0.3", {"start": v(12.7, 315.91) * mm, "end": v(0, 315.91) * mm});
            skLineSegment(sketch, "E133.0.1", {"start": v(-133.35, 214.31) * mm, "end": v(-120.65, 214.31) * mm});
            skLineSegment(sketch, "E133.0.2", {"start": v(-120.65, 214.31) * mm, "end": v(-120.65, 315.91) * mm});
            skLineSegment(sketch, "E133.0.3", {"start": v(-120.65, 315.91) * mm, "end": v(-133.35, 315.91) * mm});
            skLineSegment(sketch, "E134", {"start": v(-133.35, 1128.71) * mm, "end": v(-133.35, 315.91) * mm});
            skLineSegment(sketch, "E135", {"start": v(12.7, 315.91) * mm, "end": v(12.7, 1128.71) * mm});
            skLineSegment(sketch, "E136", {"start": v(12.7, 214.31) * mm, "end": v(12.7, 50.8) * mm});
            skLineSegment(sketch, "E137", {"start": v(-133.35, 214.31) * mm, "end": v(-133.35, 50.8) * mm});
            skLineSegment(sketch, "E138", {"start": v(-133.35, 1393.83) * mm, "end": v(-133.35, 1230.31) * mm});
            skLineSegment(sketch, "E139", {"start": v(12.7, 1393.83) * mm, "end": v(12.7, 1230.31) * mm});
            skLineSegment(sketch, "E140.0", {"start": v(-53.97, 214.31) * mm, "end": v(-53.97, 315.91) * mm});
            skLineSegment(sketch, "E141.0", {"start": v(-53.97, 315.91) * mm, "end": v(-66.67, 315.91) * mm});
            skLineSegment(sketch, "E142.0", {"start": v(-53.97, 214.31) * mm, "end": v(-66.67, 214.31) * mm});
            skLineSegment(sketch, "E143.0", {"start": v(-66.68, 1230.31) * mm, "end": v(-66.68, 1128.71) * mm});
            skLineSegment(sketch, "E144.0", {"start": v(-66.68, 1128.71) * mm, "end": v(-53.98, 1128.71) * mm});
            skLineSegment(sketch, "E145.0", {"start": v(-66.68, 1230.31) * mm, "end": v(-53.98, 1230.31) * mm});
            skLineSegment(sketch, "E146", {"start": v(-53.97, 1230.31) * mm, "end": v(-53.97, 1128.71) * mm});
            skLineSegment(sketch, "E147", {"start": v(-66.68, 315.91) * mm, "end": v(-66.68, 214.31) * mm});
            skPoint(sketch, "E148.end.orphan", {"position": v(-12.7, 31.75) * mm});
            skPoint(sketch, "E149.end.orphan", {"position": v(-107.95, 31.75) * mm});
            skLineSegment(sketch, "E150", {"start": v(-12.7, 1393.83) * mm, "end": v(-107.95, 1393.83) * mm, "construction": true});
            skLineSegment(sketch, "E151", {"start": v(-12.7, 50.8) * mm, "end": v(-107.95, 50.8) * mm, "construction": true});
            skLineSegment(sketch, "E152.0", {"start": v(-12.7, 1412.88) * mm, "end": v(-107.95, 1412.88) * mm});
            skLineSegment(sketch, "E153", {"start": v(-12.7, 1412.88) * mm, "end": v(-12.7, 1393.83) * mm});
            skLineSegment(sketch, "E154", {"start": v(-107.95, 1412.88) * mm, "end": v(-107.95, 1393.83) * mm});
            skLineSegment(sketch, "E155.0", {"start": v(-12.7, 31.75) * mm, "end": v(-107.95, 31.75) * mm});
            skLineSegment(sketch, "E156", {"start": v(-12.7, 31.75) * mm, "end": v(-12.7, 50.8) * mm});
            skLineSegment(sketch, "E157", {"start": v(-107.95, 31.75) * mm, "end": v(-107.95, 50.8) * mm});
            skSolve(sketch);
        }
        {
            var Q0;
            Q0=makeQuery(id+"F24.imprint","IMPRINT",FACE,{"disambiguationData":[TD([[makeQuery(id+"F24.imprint","IMPRINT",EDGE,{"derivedFrom":sQuery(id+"F24.wireOp",EDGE,"E121.0")}),-1.0]])]});
            var Q1;
            Q1=makeQuery(id+"F24.imprint","IMPRINT",FACE,{"disambiguationData":[TD([[makeQuery(id+"F24.imprint","IMPRINT",EDGE,{"derivedFrom":sQuery(id+"F24.wireOp",EDGE,"E131.0.1")}),1.0]])]});
            var Q2;
            {var subQ0=sQuery(id+"F24.wireOp",EDGE,"E128");Q2=makeQuery(id+"F24.imprint","IMPRINT",FACE,{"disambiguationData":[TD([[makeQuery(id+"F24.imprint","IMPRINT",EDGE,{"derivedFrom":subQ0}),-1.0]])]});}
            var Q3;
            {var subQ0=sQuery(id+"F24.wireOp",EDGE,"E126");Q3=makeQuery(id+"F24.imprint","IMPRINT",FACE,{"disambiguationData":[TD([[makeQuery(id+"F24.imprint","IMPRINT",EDGE,{"derivedFrom":subQ0}),1.0]])]});}
            extrude(context, id + "F25", {"entities" : qUnion([Q0, Q1, Q2, Q3]), "depth" : 12.7 * mm});
        }
    });
